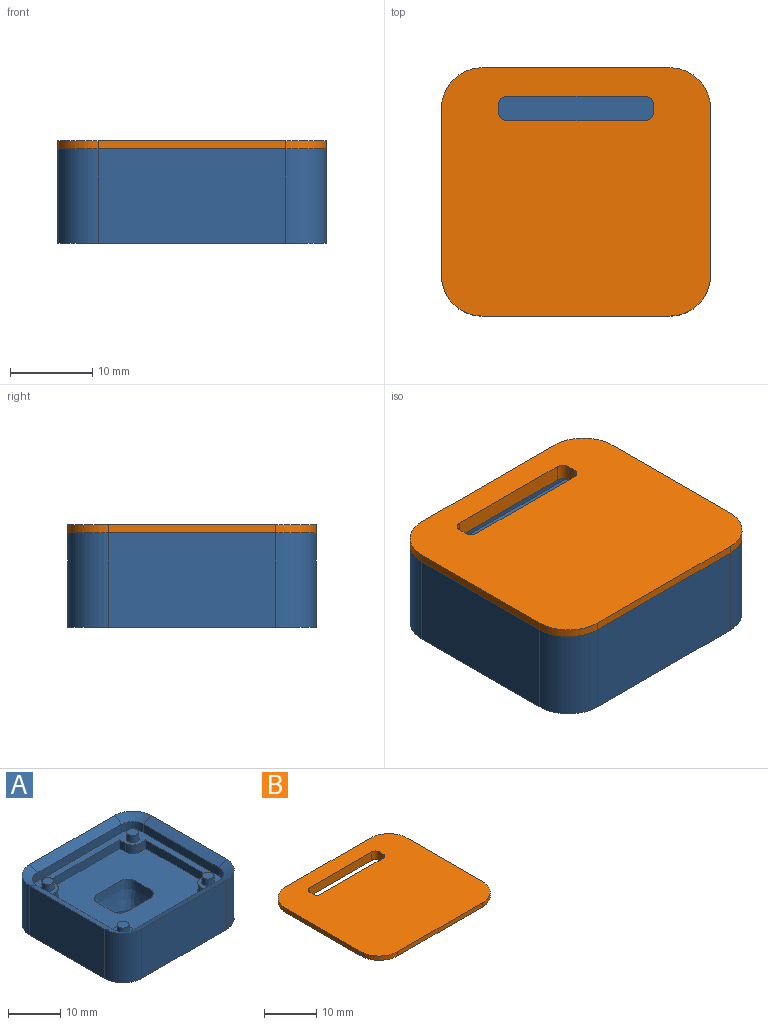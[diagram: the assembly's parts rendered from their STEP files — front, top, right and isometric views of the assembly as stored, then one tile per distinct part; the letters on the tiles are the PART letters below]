
ASSEMBLY  parts=2 mates=1
PART A: 59 faces, bbox 32.9x30.4x11.7 mm
  f0: plane 16x16mm, normal (0,0,-1), area 172.8mm2, adj f11,f13
  f1: plane 22.86x11.5mm, normal (0,-1,0), area 262.9mm2, adj f2,f8,f12,f54
  f2: cylinder r=4.94mm len=11.5mm, axis (0,0,1), area 89.2mm2, adj f1,f3,f12,f52
  f3: plane 20.32x11.5mm, normal (1,0,0), area 233.7mm2, adj f2,f4,f12,f51
  f4: cylinder r=4.94mm len=11.5mm, axis (0,0,1), area 89.2mm2, adj f3,f5,f12,f53
  f5: plane 22.86x11.5mm, normal (0,1,0), area 262.9mm2, adj f4,f6,f12,f55
  f6: cylinder r=4.94mm len=11.5mm, axis (0,0,1), area 89.2mm2, adj f5,f7,f12,f57
  f7: plane 20.32x11.5mm, normal (-1,0,0), area 233.7mm2, adj f6,f8,f12,f58
  f8: cylinder r=4.94mm len=11.5mm, axis (0,0,1), area 89.2mm2, adj f1,f7,f12,f56
  f9: plane 26.12x23.58mm, normal (0,0,1), area 482.1mm2, adj f10,f18,f19,f20,f21,f22,f23,f24
  f10: bspline ~10.2x8mm, area 176.5mm2, adj f9,f11
  f11: cylinder r=3mm len=6mm, axis (0,0,1), area 9.4mm2, adj f0,f10
  f12: plane 32.74x30.2mm, normal (0,0,-1), area 436.9mm2, adj f1,f2,f3,f4,f5,f6,f7,f8
  f13: cylinder r=8mm len=16mm, axis (0,0,-1), area 201.1mm2, adj f0,f16
  f14: cylinder r=13mm len=26mm, axis (0,0,-1), area 326.7mm2, adj f12,f17
  f15: plane 24x24mm, normal (0,0,-1), area 197.9mm2, adj f16,f17
  f16: torus R=9mm, axis (0,0,-1), area 82.5mm2, adj f13,f15
  f17: torus R=12mm, axis (0,0,-1), area 124.7mm2, adj f14,f15
  f18: cylinder r=2mm len=2mm, axis (0,0,-1), area 6.3mm2, adj f9,f19,f33,f34
  f19: plane 2x1.54mm, normal (1,0,0), area 3.1mm2, adj f9,f18,f20,f34
  f20: plane 18.86x2mm, normal (0,-1,0), area 37.7mm2, adj f9,f19,f21,f34
  f21: plane 2x1.54mm, normal (-1,0,0), area 3.1mm2, adj f9,f20,f22,f34
  f22: cylinder r=2mm len=2mm, axis (0,0,-1), area 6.3mm2, adj f9,f21,f23,f34
  f23: plane 2x1.54mm, normal (0,-1,0), area 3.1mm2, adj f9,f22,f24,f34
  f24: plane 16.32x2mm, normal (-1,0,0), area 32.6mm2, adj f9,f23,f25,f34
  f25: plane 2x1.54mm, normal (0,1,0), area 3.1mm2, adj f9,f24,f26,f34
  f26: cylinder r=2mm len=2mm, axis (0,0,-1), area 6.3mm2, adj f9,f25,f27,f34
  f27: plane 2x1.54mm, normal (-1,0,0), area 3.1mm2, adj f9,f26,f28,f34
  f28: plane 18.86x2mm, normal (0,1,0), area 37.7mm2, adj f9,f27,f29,f34
  f29: plane 2x1.54mm, normal (1,0,0), area 3.1mm2, adj f9,f28,f30,f34
  f30: cylinder r=2mm len=2mm, axis (0,0,-1), area 6.3mm2, adj f9,f29,f31,f34
  f31: plane 2x1.54mm, normal (0,1,0), area 3.1mm2, adj f9,f30,f32,f34
  f32: plane 16.32x2mm, normal (1,0,0), area 32.6mm2, adj f9,f31,f33,f34
  f33: plane 2x1.54mm, normal (0,-1,0), area 3.1mm2, adj f9,f18,f32,f34
  f34: plane 28.74x26.2mm, normal (0,0,1), area 166.6mm2, adj f18,f19,f20,f21,f22,f23,f24,f25
  f35: cone r=1.22mm half-angle=3deg, axis (0,0,-1), area 11.9mm2, adj f34,f36
  f36: plane 2.27x2.27mm, normal (0,0,1), area 4.1mm2, adj f35
  f37: cone r=1.22mm half-angle=3deg, axis (0,0,-1), area 11.9mm2, adj f34,f38
  f38: plane 2.27x2.27mm, normal (0,0,1), area 4.1mm2, adj f37
  f39: cone r=1.22mm half-angle=3deg, axis (0,0,-1), area 11.9mm2, adj f34,f40
  f40: plane 2.27x2.27mm, normal (0,0,1), area 4.1mm2, adj f39
  f41: cone r=1.22mm half-angle=3deg, axis (0,0,-1), area 11.9mm2, adj f34,f42
  f42: plane 2.27x2.27mm, normal (0,0,1), area 4.1mm2, adj f41
  f43: cylinder r=2.94mm len=2.94mm, axis (0,0,-1), area 9.2mm2, adj f34,f44,f50,f57
  f44: plane 22.86x2mm, normal (0,-1,0), area 45.7mm2, adj f34,f43,f45,f55
  f45: cylinder r=2.94mm len=2.94mm, axis (0,0,-1), area 9.2mm2, adj f34,f44,f46,f53
  f46: plane 20.32x2mm, normal (-1,0,0), area 40.6mm2, adj f34,f45,f47,f51
  f47: cylinder r=2.94mm len=2.94mm, axis (0,0,-1), area 9.2mm2, adj f34,f46,f48,f52
  f48: plane 22.86x2mm, normal (0,1,0), area 45.7mm2, adj f34,f47,f49,f54
  f49: cylinder r=2.94mm len=2.94mm, axis (0,0,-1), area 9.2mm2, adj f34,f48,f50,f56
  f50: plane 20.32x2mm, normal (1,0,0), area 40.6mm2, adj f34,f43,f49,f58
  f51: plane 20.32x2mm, normal (-0.45,0,0.89), area 45.4mm2, adj f3,f46,f52,f53
  f52: cone r=2.94mm half-angle=63.4deg, axis (0,0,1), area 13.8mm2, adj f2,f47,f51,f54
  f53: cone r=2.94mm half-angle=63.4deg, axis (0,0,1), area 13.8mm2, adj f4,f45,f51,f55
  f54: plane 22.86x2mm, normal (0,0.45,0.89), area 51.1mm2, adj f1,f48,f52,f56
  f55: plane 22.86x2mm, normal (0,-0.45,0.89), area 51.1mm2, adj f5,f44,f53,f57
  f56: cone r=2.94mm half-angle=63.4deg, axis (0,0,1), area 13.8mm2, adj f8,f49,f54,f58
  f57: cone r=2.94mm half-angle=63.4deg, axis (0,0,1), area 13.8mm2, adj f6,f43,f55,f58
  f58: plane 20.32x2mm, normal (0.45,0,0.89), area 45.4mm2, adj f7,f50,f56,f57
PART B: 26 faces, bbox 32.7x30.2x2 mm
  f0: cylinder r=1mm len=2mm, axis (0,0,-1), area 3.1mm2, adj f1,f15,f16,f17
  f1: plane 2x1mm, normal (-1,0,0), area 2mm2, adj f0,f2,f16,f17
  f2: cylinder r=1mm len=2mm, axis (0,0,-1), area 3.1mm2, adj f1,f3,f16,f17
  f3: plane 16.8x2mm, normal (0,1,0), area 33.6mm2, adj f2,f4,f16,f17
  f4: cylinder r=1mm len=2mm, axis (0,0,-1), area 3.1mm2, adj f3,f5,f16,f17
  f5: plane 2x1mm, normal (1,0,0), area 2mm2, adj f4,f6,f16,f17
  f6: cylinder r=1mm len=2mm, axis (0,0,-1), area 3.1mm2, adj f5,f15,f16,f17
  f7: cylinder r=4.94mm len=4.94mm, axis (0,0,-1), area 7.8mm2, adj f8,f14,f16,f23
  f8: plane 20.32x1mm, normal (-1,0,0), area 20.3mm2, adj f7,f9,f16,f25
  f9: cylinder r=4.94mm len=4.94mm, axis (0,0,-1), area 7.8mm2, adj f8,f10,f16,f24
  f10: plane 22.86x1mm, normal (0,-1,0), area 22.9mm2, adj f9,f11,f16,f22
  f11: cylinder r=4.94mm len=4.94mm, axis (0,0,-1), area 7.8mm2, adj f10,f12,f16,f20
  f12: plane 20.32x1mm, normal (1,0,0), area 20.3mm2, adj f11,f13,f16,f18
  f13: cylinder r=4.94mm len=4.94mm, axis (0,0,-1), area 7.8mm2, adj f12,f14,f16,f19
  f14: plane 22.86x1mm, normal (0,1,0), area 22.9mm2, adj f7,f13,f16,f21
  f15: plane 16.8x2mm, normal (0,-1,0), area 33.6mm2, adj f0,f6,f16,f17
  f16: plane 32.74x30.2mm, normal (0,0,1), area 912.3mm2, adj f0,f1,f2,f3,f4,f5,f6,f7
  f17: plane 28.74x26.2mm, normal (0,0,-1), area 690mm2, adj f0,f1,f2,f3,f4,f5,f6,f15
  f18: plane 20.32x2mm, normal (0.45,0,-0.89), area 45.4mm2, adj f12,f17,f19,f20
  f19: cone r=4.94mm half-angle=63.4deg, axis (0,0,1), area 13.8mm2, adj f13,f17,f18,f21
  f20: cone r=4.94mm half-angle=63.4deg, axis (0,0,1), area 13.8mm2, adj f11,f17,f18,f22
  f21: plane 22.86x2mm, normal (0,0.45,-0.89), area 51.1mm2, adj f14,f17,f19,f23
  f22: plane 22.86x2mm, normal (0,-0.45,-0.89), area 51.1mm2, adj f10,f17,f20,f24
  f23: cone r=4.94mm half-angle=63.4deg, axis (0,0,1), area 13.8mm2, adj f7,f17,f21,f25
  f24: cone r=4.94mm half-angle=63.4deg, axis (0,0,1), area 13.8mm2, adj f9,f17,f22,f25
  f25: plane 20.32x2mm, normal (-0.45,0,-0.89), area 45.4mm2, adj f8,f17,f23,f24
PLACE A rot(axis=(0.69,0.41,0.6),0deg) t=(-2.09,-3.77,4.71)mm
PLACE B t=(-2.09,-3.77,6.71)mm
MATE fastened B.f13 <-> A.f4  axis (0,0,-1) through (9.34,6.39,8.71)mm
